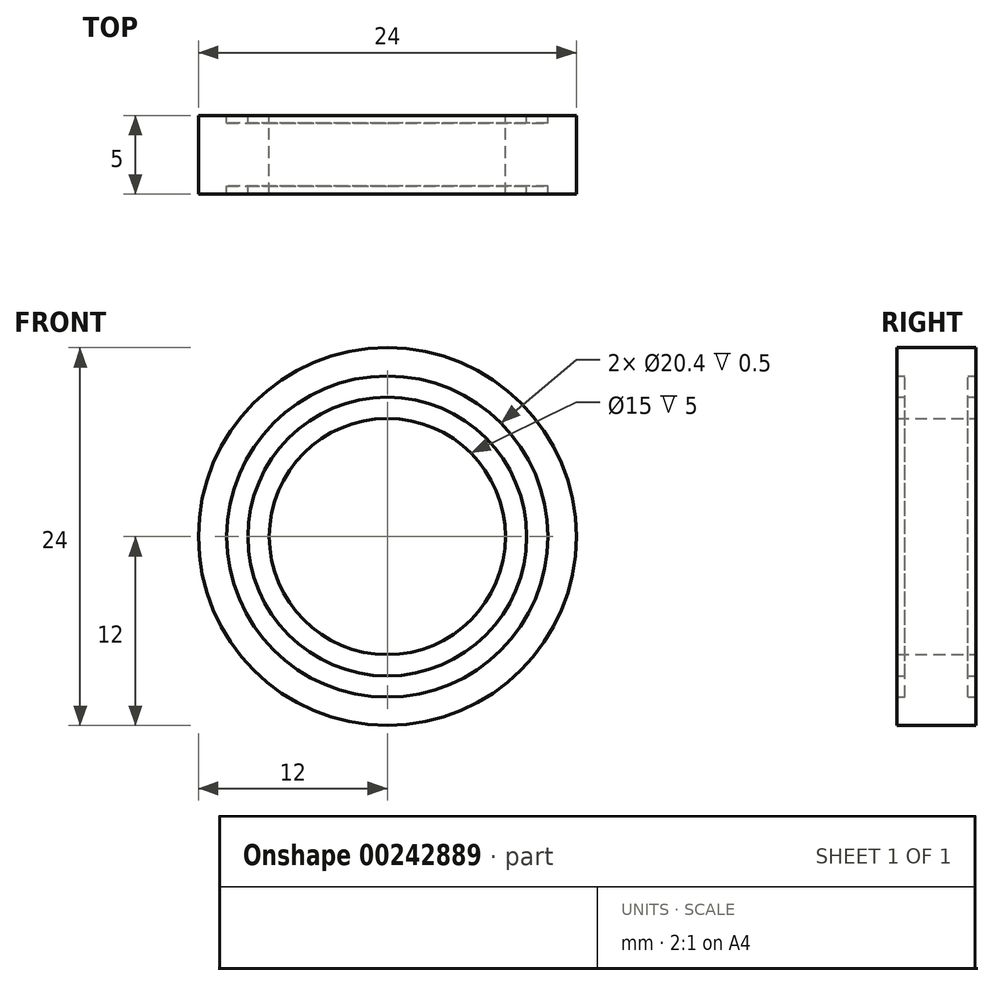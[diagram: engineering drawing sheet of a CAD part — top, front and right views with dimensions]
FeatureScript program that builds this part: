
annotation { "Feature Type Name" : "Feature", "Feature Type Description" : "" }
export const myFeature = defineFeature(function(context is Context, id is Id, definition is map)
    precondition{}
    {
        {
            assignVariable(context, id + "F0", {"name" : "T", "anyValue" : 5});
        }
        {
            var Q0;
            Q0=qCreatedBy(makeId("Front.planeOp"),FACE);
            var sketch = newSketch(context, id + "F1", { "sketchPlane" : qUnion([Q0])});
            skCircle(sketch, "E0", {"center": v(0, 0) * mm, "radius": 7.5 * mm});
            skCircle(sketch, "E1", {"center": v(0, 0) * mm, "radius": 8.85 * mm});
            skCircle(sketch, "E2", {"center": v(0, 0) * mm, "radius": 10.2 * mm});
            skCircle(sketch, "E3", {"center": v(0, 0) * mm, "radius": 12 * mm});
            skSolve(sketch);
        }
        {
            var Q0;
            Q0=makeQuery(id+"F1.imprint","IMPRINT",FACE,{"disambiguationData":[TD([[makeQuery(id+"F1.imprint","IMPRINT",EDGE,{"derivedFrom":sQuery(id+"F1.wireOp",EDGE,"E1")}),-1.0]])]});
            extrude(context, id + "F2", {"entities" : qUnion([Q0]), "endBound" : BoundingType.SYMMETRIC, "depth" : (getVariable(context, 'T') - 1) * mm});
        }
        {
            var Q0;
            Q0=makeQuery(id+"F1.imprint","IMPRINT",FACE,{"disambiguationData":[TD([[makeQuery(id+"F1.imprint","IMPRINT",EDGE,{"derivedFrom":sQuery(id+"F1.wireOp",EDGE,"E0")}),-1.0]])]});
            var Q1;
            Q1=makeQuery(id+"F1.imprint","IMPRINT",FACE,{"disambiguationData":[TD([[makeQuery(id+"F1.imprint","IMPRINT",EDGE,{"derivedFrom":sQuery(id+"F1.wireOp",EDGE,"E2")}),-1.0]])]});
            extrude(context, id + "F3", {"entities" : qUnion([Q0, Q1]), "operationType" : NewBodyOperationType.ADD, "endBound" : BoundingType.SYMMETRIC, "depth" : (getVariable(context, 'T')) * mm});
        }
    });
